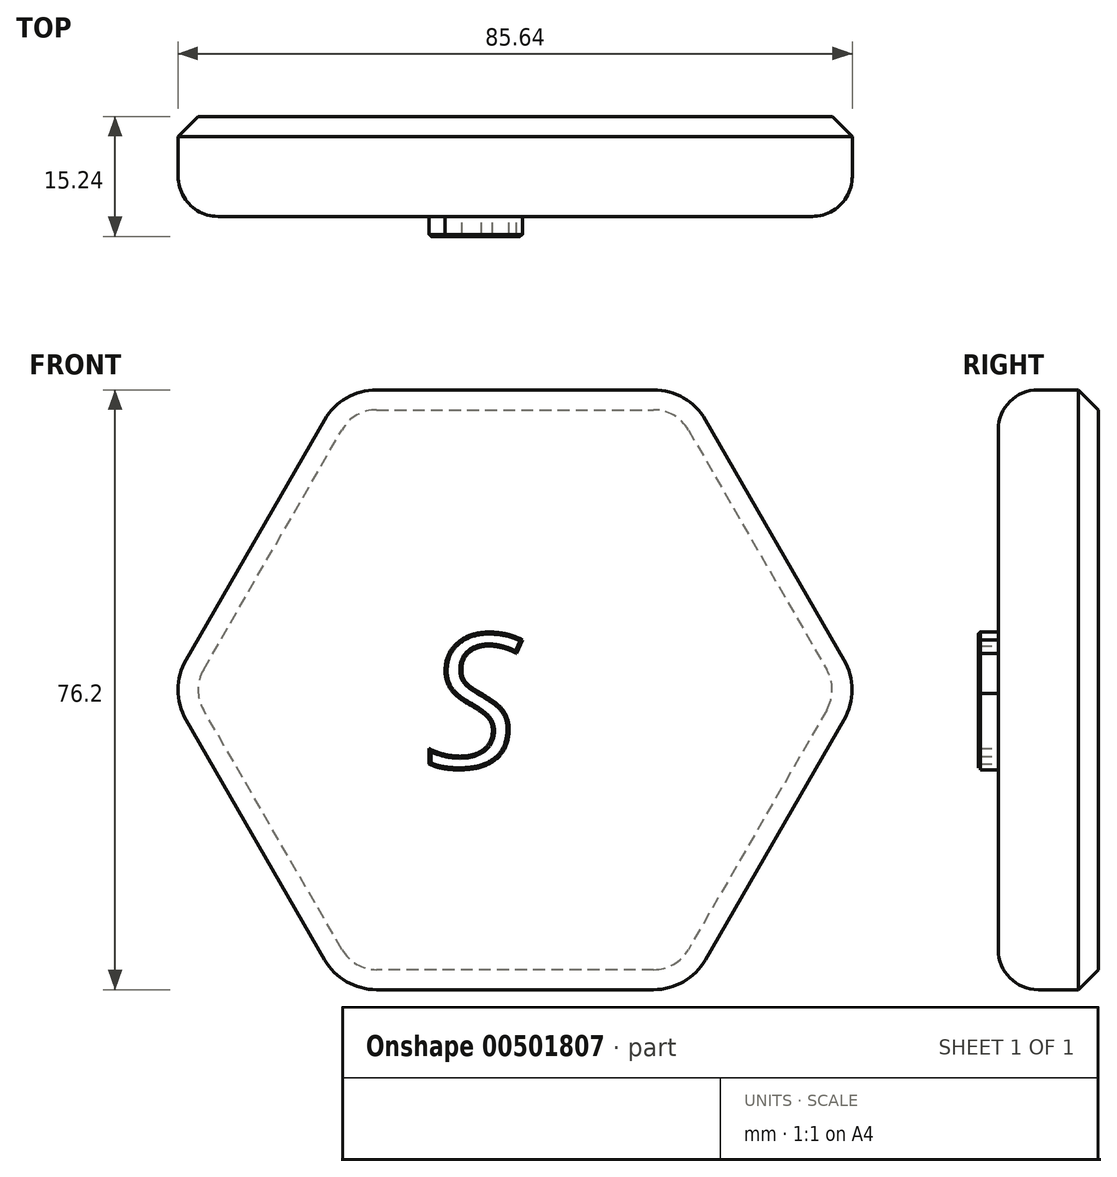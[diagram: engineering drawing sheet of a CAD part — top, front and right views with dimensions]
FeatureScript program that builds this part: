
annotation { "Feature Type Name" : "Feature", "Feature Type Description" : "" }
export const myFeature = defineFeature(function(context is Context, id is Id, definition is map)
    precondition{}
    {
        {
            var Q0;
            Q0=qCreatedBy(makeId("Front.planeOp"),FACE);
            var sketch = newSketch(context, id + "F0", { "sketchPlane" : qUnion([Q0])});
            skCircle(sketch, "E0.cCircle", {"center": v(0, 0) * mm, "radius": 38.1 * mm, "construction": true});
            skLineSegment(sketch, "E0.0", {"start": v(22, -38.1) * mm, "end": v(-22, -38.1) * mm});
            skLineSegment(sketch, "E0.1", {"start": v(-22, -38.1) * mm, "end": v(-44, 0) * mm});
            skLineSegment(sketch, "E0.2", {"start": v(-44, 0) * mm, "end": v(-22, 38.1) * mm});
            skLineSegment(sketch, "E0.3", {"start": v(-22, 38.1) * mm, "end": v(22, 38.1) * mm});
            skLineSegment(sketch, "E0.4", {"start": v(22, 38.1) * mm, "end": v(44, 0) * mm});
            skLineSegment(sketch, "E0.5", {"start": v(44, 0) * mm, "end": v(22, -38.1) * mm});
            skPoint(sketch, "E0.0.midPoint", {"position": v(0, -38.1) * mm});
            skSolve(sketch);
        }
        {
            var Q0;
            Q0=makeQuery(id+"F0.imprint","IMPRINT",FACE,{"disambiguationData":[TD([[makeQuery(id+"F0.imprint","IMPRINT",EDGE,{"derivedFrom":sQuery(id+"F0.wireOp",EDGE,"E0.0")}),-1.0]])]});
            extrude(context, id + "F1", {"entities" : qUnion([Q0]), "depth" : 12.7 * mm});
        }
        {
            var Q0;
            Q0=makeQuery(id+"F1.opExtrude","SWEPT_EDGE",EDGE,{"disambiguationData":[OSD([sQuery(id+"F0.wireOp",EDGE,"E0.1"),sQuery(id+"F0.wireOp",EDGE,"E0.2")])]});
            var Q1;
            Q1=makeQuery(id+"F1.opExtrude","SWEPT_EDGE",EDGE,{"disambiguationData":[OSD([sQuery(id+"F0.wireOp",EDGE,"E0.4"),sQuery(id+"F0.wireOp",EDGE,"E0.5")])]});
            var Q2;
            Q2=makeQuery(id+"F1.opExtrude","SWEPT_EDGE",EDGE,{"disambiguationData":[OSD([sQuery(id+"F0.wireOp",EDGE,"E0.2"),sQuery(id+"F0.wireOp",EDGE,"E0.3")])]});
            var Q3;
            Q3=makeQuery(id+"F1.opExtrude","SWEPT_EDGE",EDGE,{"disambiguationData":[OSD([sQuery(id+"F0.wireOp",EDGE,"E0.0"),sQuery(id+"F0.wireOp",EDGE,"E0.1")])]});
            var Q4;
            Q4=makeQuery(id+"F1.opExtrude","SWEPT_EDGE",EDGE,{"disambiguationData":[OSD([sQuery(id+"F0.wireOp",EDGE,"E0.3"),sQuery(id+"F0.wireOp",EDGE,"E0.4")])]});
            var Q5;
            Q5=makeQuery(id+"F1.opExtrude","SWEPT_EDGE",EDGE,{"disambiguationData":[OSD([sQuery(id+"F0.wireOp",EDGE,"E0.0"),sQuery(id+"F0.wireOp",EDGE,"E0.5")])]});
            fillet(context, id + "F2", {"entities" : qUnion([Q0, Q1, Q2, Q3, Q4, Q5]), "radius" : 7.62 * mm, "tangentPropagation" : true, "allowEdgeOverflow" : false});
        }
        {
            var Q0;
            Q0=makeQuery(id+"F1.opExtrude","CAP_EDGE",EDGE,{"disambiguationData":[OSD([sQuery(id+"F0.wireOp",EDGE,"E0.1")])],"isStart":false});
            var Q1;
            Q1=makeQuery(id+"F1.opExtrude","CAP_EDGE",EDGE,{"disambiguationData":[OSD([sQuery(id+"F0.wireOp",EDGE,"E0.5")])],"isStart":false});
            var Q2;
            Q2=makeQuery(id+"F1.opExtrude","CAP_EDGE",EDGE,{"disambiguationData":[OSD([sQuery(id+"F0.wireOp",EDGE,"E0.2")])],"isStart":false});
            var Q3;
            {var subQ0=sQuery(id+"F0.wireOp",EDGE,"E0.1");var subQ1=sQuery(id+"F0.wireOp",EDGE,"E0.0");Q3=makeQuery(id+"F2.opFillet","BLEND_EDGE",EDGE,{"blendedFrom":[makeQuery(id+"F1.opExtrude","SWEPT_EDGE",EDGE,{"disambiguationData":[OSD([subQ1,subQ0])]}),makeQuery(id+"F1.opExtrude","CAP_FACE",FACE,{"disambiguationData":[OSD([subQ1,subQ0,sQuery(id+"F0.wireOp",EDGE,"E0.2"),sQuery(id+"F0.wireOp",EDGE,"E0.3"),sQuery(id+"F0.wireOp",EDGE,"E0.4"),sQuery(id+"F0.wireOp",EDGE,"E0.5")])],"isStart":false})],"blendedInto":[makeQuery(id+"F1.opExtrude","CAP_FACE",FACE,{"disambiguationData":[OSD([subQ1,subQ0,sQuery(id+"F0.wireOp",EDGE,"E0.2"),sQuery(id+"F0.wireOp",EDGE,"E0.3"),sQuery(id+"F0.wireOp",EDGE,"E0.4"),sQuery(id+"F0.wireOp",EDGE,"E0.5")])],"isStart":false})]});}
            var Q4;
            {var subQ0=sQuery(id+"F0.wireOp",EDGE,"E0.3");var subQ1=sQuery(id+"F0.wireOp",EDGE,"E0.2");Q4=makeQuery(id+"F2.opFillet","BLEND_EDGE",EDGE,{"blendedFrom":[makeQuery(id+"F1.opExtrude","SWEPT_EDGE",EDGE,{"disambiguationData":[OSD([subQ1,subQ0])]}),makeQuery(id+"F1.opExtrude","CAP_FACE",FACE,{"disambiguationData":[OSD([sQuery(id+"F0.wireOp",EDGE,"E0.0"),sQuery(id+"F0.wireOp",EDGE,"E0.1"),subQ1,subQ0,sQuery(id+"F0.wireOp",EDGE,"E0.4"),sQuery(id+"F0.wireOp",EDGE,"E0.5")])],"isStart":false})],"blendedInto":[makeQuery(id+"F1.opExtrude","CAP_FACE",FACE,{"disambiguationData":[OSD([sQuery(id+"F0.wireOp",EDGE,"E0.0"),sQuery(id+"F0.wireOp",EDGE,"E0.1"),subQ1,subQ0,sQuery(id+"F0.wireOp",EDGE,"E0.4"),sQuery(id+"F0.wireOp",EDGE,"E0.5")])],"isStart":false})]});}
            var Q5;
            Q5=makeQuery(id+"F1.opExtrude","CAP_EDGE",EDGE,{"disambiguationData":[OSD([sQuery(id+"F0.wireOp",EDGE,"E0.0")])],"isStart":false});
            var Q6;
            Q6=makeQuery(id+"F1.opExtrude","CAP_EDGE",EDGE,{"disambiguationData":[OSD([sQuery(id+"F0.wireOp",EDGE,"E0.4")])],"isStart":false});
            var Q7;
            {var subQ0=sQuery(id+"F0.wireOp",EDGE,"E0.5");var subQ1=sQuery(id+"F0.wireOp",EDGE,"E0.4");Q7=makeQuery(id+"F2.opFillet","BLEND_EDGE",EDGE,{"blendedFrom":[makeQuery(id+"F1.opExtrude","SWEPT_EDGE",EDGE,{"disambiguationData":[OSD([subQ1,subQ0])]}),makeQuery(id+"F1.opExtrude","CAP_FACE",FACE,{"disambiguationData":[OSD([sQuery(id+"F0.wireOp",EDGE,"E0.0"),sQuery(id+"F0.wireOp",EDGE,"E0.1"),sQuery(id+"F0.wireOp",EDGE,"E0.2"),sQuery(id+"F0.wireOp",EDGE,"E0.3"),subQ1,subQ0])],"isStart":false})],"blendedInto":[makeQuery(id+"F1.opExtrude","CAP_FACE",FACE,{"disambiguationData":[OSD([sQuery(id+"F0.wireOp",EDGE,"E0.0"),sQuery(id+"F0.wireOp",EDGE,"E0.1"),sQuery(id+"F0.wireOp",EDGE,"E0.2"),sQuery(id+"F0.wireOp",EDGE,"E0.3"),subQ1,subQ0])],"isStart":false})]});}
            var Q8;
            {var subQ0=sQuery(id+"F0.wireOp",EDGE,"E0.2");var subQ1=sQuery(id+"F0.wireOp",EDGE,"E0.1");Q8=makeQuery(id+"F2.opFillet","BLEND_EDGE",EDGE,{"blendedFrom":[makeQuery(id+"F1.opExtrude","SWEPT_EDGE",EDGE,{"disambiguationData":[OSD([subQ1,subQ0])]}),makeQuery(id+"F1.opExtrude","CAP_FACE",FACE,{"disambiguationData":[OSD([sQuery(id+"F0.wireOp",EDGE,"E0.0"),subQ1,subQ0,sQuery(id+"F0.wireOp",EDGE,"E0.3"),sQuery(id+"F0.wireOp",EDGE,"E0.4"),sQuery(id+"F0.wireOp",EDGE,"E0.5")])],"isStart":false})],"blendedInto":[makeQuery(id+"F1.opExtrude","CAP_FACE",FACE,{"disambiguationData":[OSD([sQuery(id+"F0.wireOp",EDGE,"E0.0"),subQ1,subQ0,sQuery(id+"F0.wireOp",EDGE,"E0.3"),sQuery(id+"F0.wireOp",EDGE,"E0.4"),sQuery(id+"F0.wireOp",EDGE,"E0.5")])],"isStart":false})]});}
            var Q9;
            Q9=makeQuery(id+"F1.opExtrude","CAP_EDGE",EDGE,{"disambiguationData":[OSD([sQuery(id+"F0.wireOp",EDGE,"E0.3")])],"isStart":false});
            var Q10;
            {var subQ0=sQuery(id+"F0.wireOp",EDGE,"E0.4");var subQ1=sQuery(id+"F0.wireOp",EDGE,"E0.3");Q10=makeQuery(id+"F2.opFillet","BLEND_EDGE",EDGE,{"blendedFrom":[makeQuery(id+"F1.opExtrude","SWEPT_EDGE",EDGE,{"disambiguationData":[OSD([subQ1,subQ0])]}),makeQuery(id+"F1.opExtrude","CAP_FACE",FACE,{"disambiguationData":[OSD([sQuery(id+"F0.wireOp",EDGE,"E0.0"),sQuery(id+"F0.wireOp",EDGE,"E0.1"),sQuery(id+"F0.wireOp",EDGE,"E0.2"),subQ1,subQ0,sQuery(id+"F0.wireOp",EDGE,"E0.5")])],"isStart":false})],"blendedInto":[makeQuery(id+"F1.opExtrude","CAP_FACE",FACE,{"disambiguationData":[OSD([sQuery(id+"F0.wireOp",EDGE,"E0.0"),sQuery(id+"F0.wireOp",EDGE,"E0.1"),sQuery(id+"F0.wireOp",EDGE,"E0.2"),subQ1,subQ0,sQuery(id+"F0.wireOp",EDGE,"E0.5")])],"isStart":false})]});}
            var Q11;
            {var subQ0=sQuery(id+"F0.wireOp",EDGE,"E0.5");var subQ1=sQuery(id+"F0.wireOp",EDGE,"E0.0");Q11=makeQuery(id+"F2.opFillet","BLEND_EDGE",EDGE,{"blendedFrom":[makeQuery(id+"F1.opExtrude","SWEPT_EDGE",EDGE,{"disambiguationData":[OSD([subQ1,subQ0])]}),makeQuery(id+"F1.opExtrude","CAP_FACE",FACE,{"disambiguationData":[OSD([subQ1,sQuery(id+"F0.wireOp",EDGE,"E0.1"),sQuery(id+"F0.wireOp",EDGE,"E0.2"),sQuery(id+"F0.wireOp",EDGE,"E0.3"),sQuery(id+"F0.wireOp",EDGE,"E0.4"),subQ0])],"isStart":false})],"blendedInto":[makeQuery(id+"F1.opExtrude","CAP_FACE",FACE,{"disambiguationData":[OSD([subQ1,sQuery(id+"F0.wireOp",EDGE,"E0.1"),sQuery(id+"F0.wireOp",EDGE,"E0.2"),sQuery(id+"F0.wireOp",EDGE,"E0.3"),sQuery(id+"F0.wireOp",EDGE,"E0.4"),subQ0])],"isStart":false})]});}
            fillet(context, id + "F3", {"entities" : qUnion([Q0, Q1, Q2, Q3, Q4, Q5, Q6, Q7, Q8, Q9, Q10, Q11]), "radius" : 5.08 * mm, "tangentPropagation" : true, "allowEdgeOverflow" : false});
        }
        {
            var Q0;
            Q0=makeQuery(id+"F1.opExtrude","CAP_FACE",FACE,{"disambiguationData":[OSD([sQuery(id+"F0.wireOp",EDGE,"E0.0"),sQuery(id+"F0.wireOp",EDGE,"E0.1"),sQuery(id+"F0.wireOp",EDGE,"E0.2"),sQuery(id+"F0.wireOp",EDGE,"E0.3"),sQuery(id+"F0.wireOp",EDGE,"E0.4"),sQuery(id+"F0.wireOp",EDGE,"E0.5")])],"isStart":false});
            var sketch = newSketch(context, id + "F4", { "sketchPlane" : qUnion([Q0])});
            skText(sketch, "E1", { "text": "S", "fontName": "OpenSans-Italic.ttf"});
            const initialGuessF4  = {"E1": [-0.0114, -0.00994, 1, 0, 0.01717]};
            skSetInitialGuess(sketch, initialGuessF4);
            skSolve(sketch);
        }
        {
            var Q0;
            Q0=makeQuery(id+"F4.imprint","IMPRINT",FACE,{"disambiguationData":[TD([[makeQuery(id+"F4.imprint","IMPRINT",EDGE,{"derivedFrom":sQuery(id+"F4.wireOp",EDGE,"E1.sketch_text.stroke-0")}),-1.0]])]});
            extrude(context, id + "F5", {"entities" : qUnion([Q0]), "operationType" : NewBodyOperationType.ADD, "depth" : 2.54 * mm});
        }
        {
            var Q0;
            Q0=makeQuery(id+"F5.opExtrude","CAP_EDGE",EDGE,{"disambiguationData":[OSD([sQuery(id+"F4.wireOp",EDGE,"E1.sketch_text.stroke-1")])],"isStart":false});
            var Q1;
            Q1=makeQuery(id+"F5.opExtrude","CAP_EDGE",EDGE,{"disambiguationData":[OSD([sQuery(id+"F4.wireOp",EDGE,"E1.sketch_text.stroke-19")])],"isStart":false});
            var Q2;
            Q2=makeQuery(id+"F5.opExtrude","CAP_EDGE",EDGE,{"disambiguationData":[OSD([sQuery(id+"F4.wireOp",EDGE,"E1.sketch_text.stroke-20")])],"isStart":false});
            var Q3;
            Q3=makeQuery(id+"F5.opExtrude","CAP_EDGE",EDGE,{"disambiguationData":[OSD([sQuery(id+"F4.wireOp",EDGE,"E1.sketch_text.stroke-16")])],"isStart":false});
            var Q4;
            Q4=makeQuery(id+"F5.opExtrude","CAP_EDGE",EDGE,{"disambiguationData":[OSD([sQuery(id+"F4.wireOp",EDGE,"E1.sketch_text.stroke-15")])],"isStart":false});
            var Q5;
            Q5=makeQuery(id+"F5.opExtrude","CAP_EDGE",EDGE,{"disambiguationData":[OSD([sQuery(id+"F4.wireOp",EDGE,"E1.sketch_text.stroke-4")])],"isStart":false});
            chamfer(context, id + "F6", {"entities" : qUnion([Q0, Q1, Q2, Q3, Q4, Q5]), "width" : 0.25 * mm, "tangentPropagation" : true});
        }
        {
            var Q0;
            Q0=makeQuery(id+"F1.opExtrude","CAP_EDGE",EDGE,{"disambiguationData":[OSD([sQuery(id+"F0.wireOp",EDGE,"E0.0")])],"isStart":true});
            chamfer(context, id + "F7", {"entities" : qUnion([Q0]), "width" : 2.54 * mm, "tangentPropagation" : true});
        }
        {
            var Q0;
            Q0=makeQuery(id+"F1.opExtrude","CAP_FACE",FACE,{"disambiguationData":[OSD([sQuery(id+"F0.wireOp",EDGE,"E0.0"),sQuery(id+"F0.wireOp",EDGE,"E0.1"),sQuery(id+"F0.wireOp",EDGE,"E0.2"),sQuery(id+"F0.wireOp",EDGE,"E0.3"),sQuery(id+"F0.wireOp",EDGE,"E0.4"),sQuery(id+"F0.wireOp",EDGE,"E0.5")])],"isStart":false});
            var sketch = newSketch(context, id + "F8", { "sketchPlane" : qUnion([Q0])});
            skEllipse(sketch, "E2", {"center": v(0, -14.1) * mm, "majorRadius": 6.15 * mm, "minorRadius": 3.44 * mm, "majorAxis": v(0.84, 0.54)});
            skSolve(sketch);
        }
        {
            var Q0;
            Q0=sQuery(id+"F8.wireOp",EDGE,"E2");
            extrude(context, id + "F9", {"bodyType" : ToolBodyType.SURFACE, "surfaceEntities" : qUnion([Q0]), "oppositeDirection" : true, "depth" : 25.4 * mm});
        }
    });
